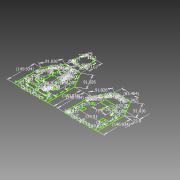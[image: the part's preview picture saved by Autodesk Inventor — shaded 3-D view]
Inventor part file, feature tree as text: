
AUTODESK INVENTOR PART (.ipt)
format: ipt  version: 2012 (Build 160160000, 160)  size: 270,336 bytes
history: native  units: mm
features: sketch x1
ambient origin geometry x8: Origin, YZ Plane, XZ Plane, XY Plane, X Axis, Y Axis, Z Axis, Center Point
feature tree (1):
  sketch  "Sketch1"  dims[d266=10.0mm d272=15.0mm d273=2.0mm d274=15.0mm d275=18.0mm d276=15.0mm d277=17.0mm d286=15.0mm d287=18.0mm d290=3.0mm d291=3.0mm d292=3.0mm d293=3.0mm d294=3.0mm d295=-5.117mm d296=10.0mm d297=15.117mm d298=10.0mm d299=5.554212mm d300=5.0mm d301=5.0mm d302=5.554212mm d303=5.554212mm d304=5.0mm d305=5.0mm d306=3.0mm d307=3.0mm d308=3.0mm d309=5.117mm d310=0.0mm d311=15.117007mm d312=3.0mm d313=5.0mm d314=5.0mm d315=5.0mm d316=5.000007mm d317=5.0mm d318=57.0mm d319=67.0mm d320=3.0mm d321=3.0mm d322=3.0mm d323=51.0mm d324=51.0mm d325=51.0mm d326=51.0mm d327=3.0mm d328=2.0mm d329=12.0mm d330=12.0mm d331=11.0mm d332=11.0mm d333=3.0mm d334=3.0mm d335=3.0mm d336=2.0mm d337=12.0mm d338=12.0mm d339=11.0mm d341=3.0mm d389=95.933639mm d391=50.0mm d392=60.0mm d393=5.0mm d394=110.0mm d395=20.0mm d396=10.0mm d397=5.0mm d398=27.4mm d399=40.4mm d400=3.0mm d401=3.0mm d402=23.7mm d403=39.8mm d404=30.0mm d405=30.0mm d406=5.0mm d407=3.0mm d408=120.0deg d409=219.764931mm d410=174.51mm d411=120.0deg d412=150.0deg d413=150.0deg d414=91.026319mm d415=91.026319mm d416=83.483681mm d417=140.933826mm d418=140.933826mm d517=10.0mm d518=2.0mm d519=10.0mm d520=2.0mm d521=10.0mm d522=2.0mm d523=10.0mm d524=2.0mm d525=10.0mm d526=2.0mm d527=15.0mm d528=15.0mm d529=15.0mm d530=15.0mm d531=15.0mm d532=15.0mm d533=10.000138mm d534=3.0mm d535=15.0mm d536=10.0mm d537=2.0mm d538=10.0mm d539=10.0mm d540=2.0mm d541=10.0mm d542=10.0mm d543=2.0mm d544=10.0mm d545=2.0mm d546=10.0mm d547=2.0mm d548=10.0mm d549=2.0mm d550=10.0mm d551=15.0mm d552=2.0mm d553=15.0mm d554=18.0mm d555=15.0mm d556=17.0mm d557=2.0mm d558=15.0mm d559=15.0mm d560=15.0mm d561=15.0mm d562=15.0mm d563=15.0mm d564=15.0mm d565=18.0mm d566=3.0mm d567=71.8mm d568=25.8mm d569=16.0mm d570=25.0mm d571=13.0mm d572=21.0mm d573=40.0mm d574=9.7mm d575=20.0mm d576=120.0deg d577=174.51mm d578=120.0deg d579=150.0deg d580=150.0deg d581=91.026319mm d582=91.026319mm d583=83.483681mm d584=140.933826mm d585=140.933826mm d586=9.0mm d587=9.0mm d588=8.999813mm d589=10.000138mm d590=19.836667mm d591=18.0mm d592=18.0mm d593=3.0mm d594=9.000166mm d595=15.0mm d596=18.0mm d597=18.0mm d598=10.0mm d599=2.0mm d600=10.0mm d601=10.0mm d602=2.0mm d603=10.0mm d604=18.0mm d605=17.933826mm d606=19.673333mm d607=7.0mm d608=15.52235mm d609=9.0mm d610=21.354415mm d611=16.742mm d612=16.741543mm]
